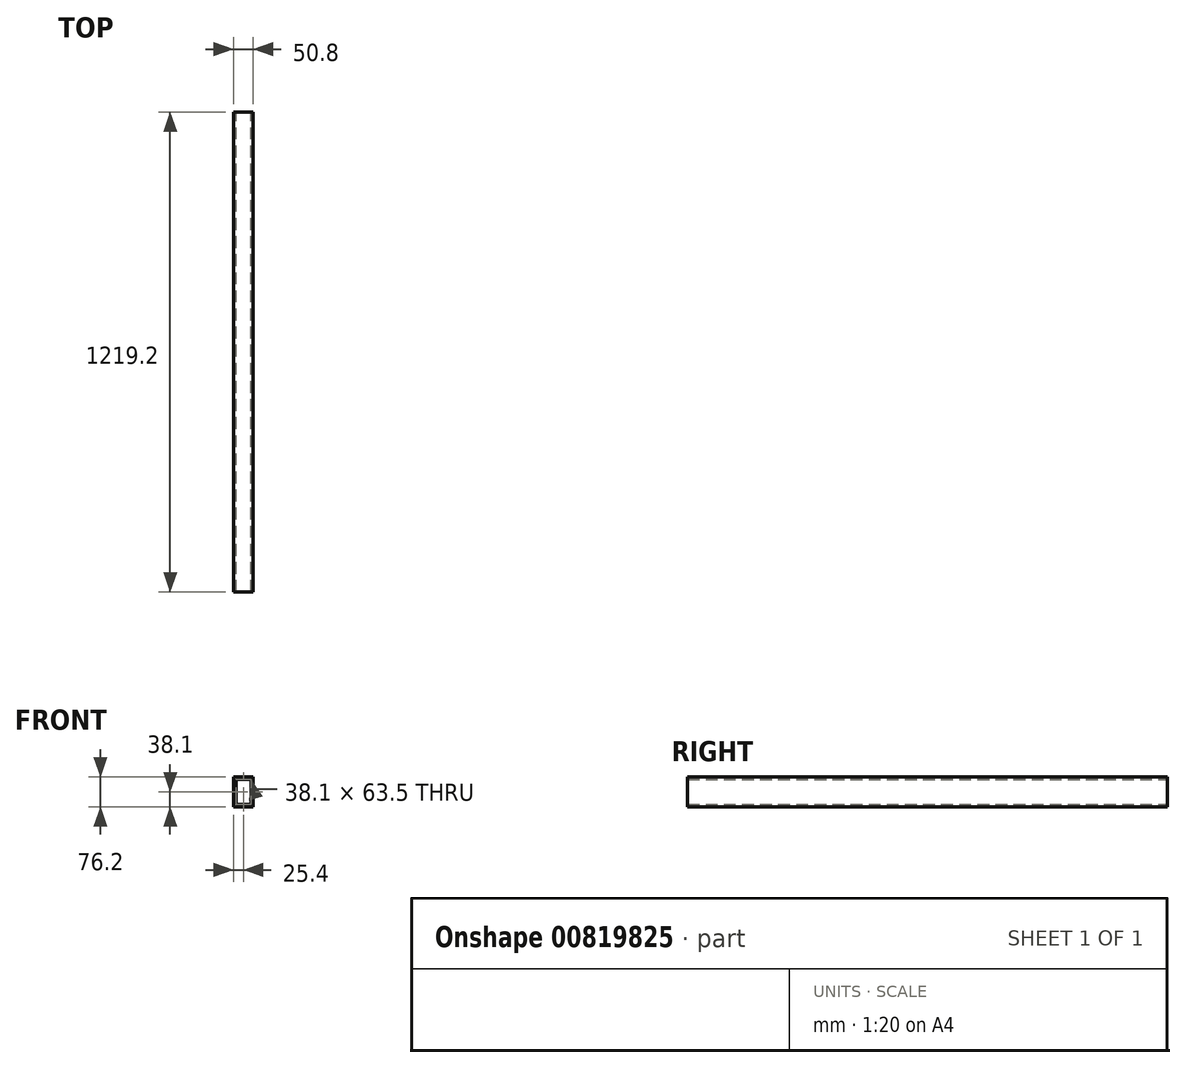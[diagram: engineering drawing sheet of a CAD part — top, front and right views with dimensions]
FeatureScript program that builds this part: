
annotation { "Feature Type Name" : "Feature", "Feature Type Description" : "" }
export const myFeature = defineFeature(function(context is Context, id is Id, definition is map)
    precondition{}
    {
        {
            var Q0;
            Q0=qCreatedBy(makeId("Front.planeOp"),FACE);
            var sketch = newSketch(context, id + "F0", { "sketchPlane" : qUnion([Q0])});
            skLineSegment(sketch, "E0.bottom", {"start": v(25.4, 38.1) * mm, "end": v(-25.4, 38.1) * mm});
            skLineSegment(sketch, "E0.top", {"start": v(25.4, -38.1) * mm, "end": v(-25.4, -38.1) * mm});
            skLineSegment(sketch, "E0.left", {"start": v(25.4, 38.1) * mm, "end": v(25.4, -38.1) * mm});
            skLineSegment(sketch, "E0.right", {"start": v(-25.4, 38.1) * mm, "end": v(-25.4, -38.1) * mm});
            skPoint(sketch, "E0.middle", {"position": v(0, 0) * mm});
            skLineSegment(sketch, "E1.bottom", {"start": v(19.05, -31.75) * mm, "end": v(-19.05, -31.75) * mm});
            skLineSegment(sketch, "E1.top", {"start": v(19.05, 31.75) * mm, "end": v(-19.05, 31.75) * mm});
            skLineSegment(sketch, "E1.left", {"start": v(-19.05, -31.75) * mm, "end": v(-19.05, 31.75) * mm});
            skLineSegment(sketch, "E1.right", {"start": v(19.05, -31.75) * mm, "end": v(19.05, 31.75) * mm});
            skSolve(sketch);
        }
        {
            var Q0;
            Q0=makeQuery(id+"F0.imprint","IMPRINT",FACE,{"disambiguationData":[TD([[makeQuery(id+"F0.imprint","IMPRINT",EDGE,{"derivedFrom":sQuery(id+"F0.wireOp",EDGE,"E0.bottom")}),1.0]])]});
            extrude(context, id + "F1", {"entities" : qUnion([Q0]), "depth" : 1219.2 * mm, "offsetDistance" : 25.4 * mm});
        }
    });
